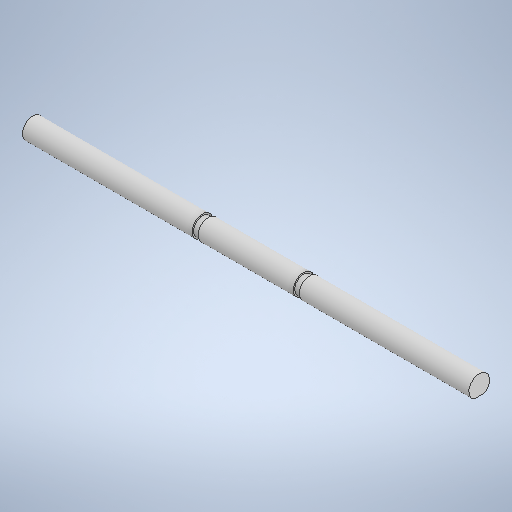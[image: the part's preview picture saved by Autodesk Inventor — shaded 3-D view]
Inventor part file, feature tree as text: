
AUTODESK INVENTOR PART (.ipt)
format: ipt  version: 2025.2 (Build 292293000, 293)  size: 264,704 bytes
history: native  units: mm
features: extrude x2, sketch x1, plane x1, mirror x1
ambient origin geometry x8: Origin, YZ Plane, XZ Plane, XY Plane, X Axis, Y Axis, Z Axis, Center Point
bodies: Solid1 (feature_tree)
feature tree (5):
  sketch  "Sketch1"  dims[d0=7.0mm d1=150.0mm d2=0.0mm d3=0.5mm d6=16.0mm d7=2.0mm d8=0.0mm d9=3.0mm]
  extrude  "Extrusion1"  Depth=150.0mm TaperAngle=0.0deg
  plane  "Work Plane1"
  extrude  "Extrusion3"  Depth=3.0mm
  mirror  "Mirror1"
